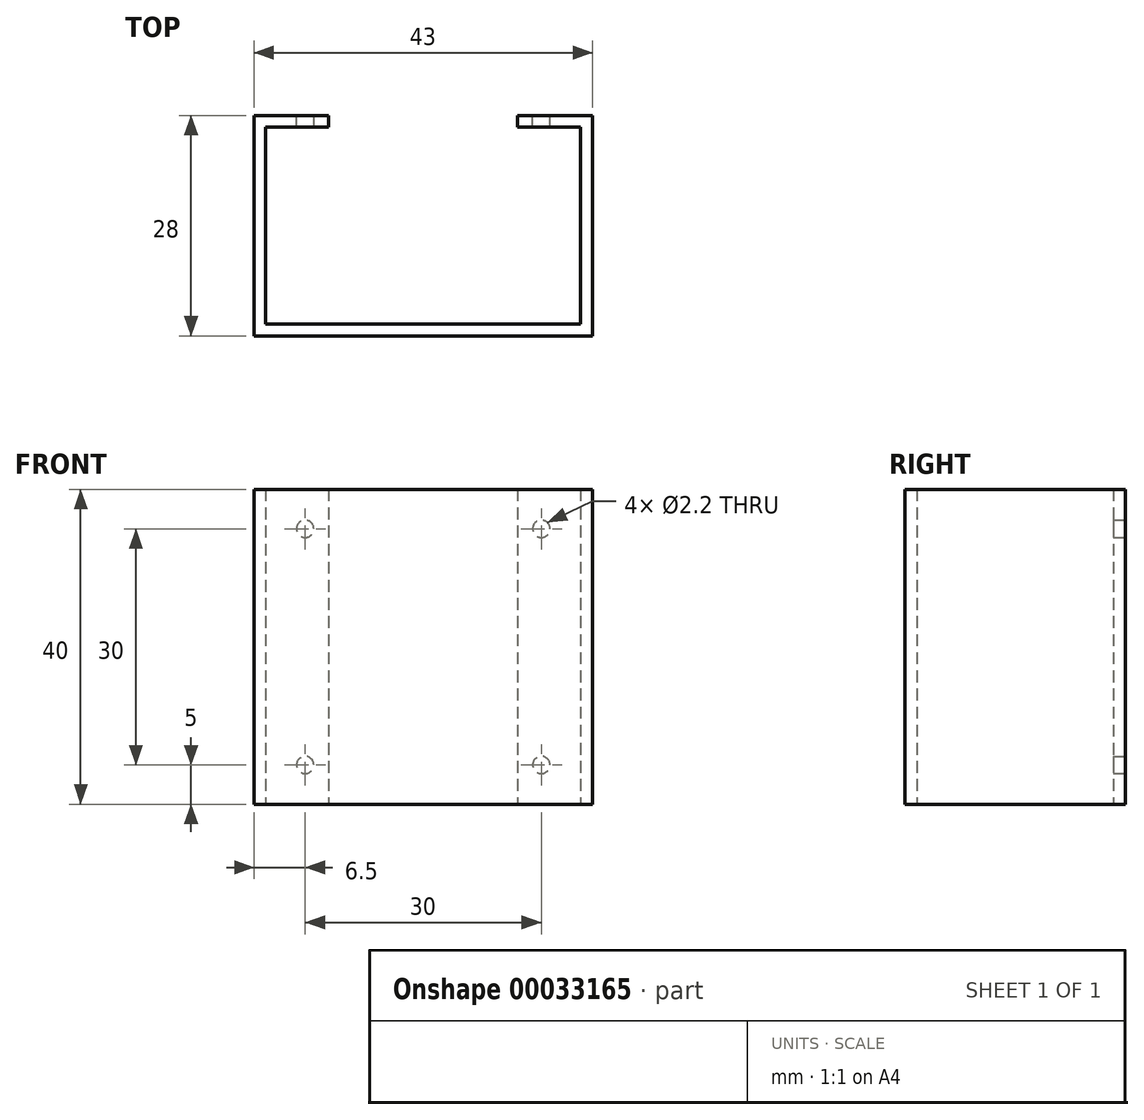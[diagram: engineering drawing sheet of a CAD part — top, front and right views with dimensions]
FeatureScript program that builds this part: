
annotation { "Feature Type Name" : "Feature", "Feature Type Description" : "" }
export const myFeature = defineFeature(function(context is Context, id is Id, definition is map)
    precondition{}
    {
        {
            var Q0;
            Q0=qCreatedBy(makeId("Top.planeOp"),FACE);
            var sketch = newSketch(context, id + "F0", { "sketchPlane" : qUnion([Q0])});
            skLineSegment(sketch, "E0.bottom", {"start": v(-21.5, 14) * mm, "end": v(-12, 14) * mm});
            skLineSegment(sketch, "E0.top", {"start": v(-21.5, -14) * mm, "end": v(21.5, -14) * mm});
            skLineSegment(sketch, "E0.left", {"start": v(-21.5, 14) * mm, "end": v(-21.5, -14) * mm});
            skLineSegment(sketch, "E0.right", {"start": v(21.5, 14) * mm, "end": v(21.5, -14) * mm});
            skPoint(sketch, "E0.middle", {"position": v(0, 0) * mm});
            skLineSegment(sketch, "E1.bottom", {"start": v(-20, 12.5) * mm, "end": v(-12, 12.5) * mm});
            skLineSegment(sketch, "E1.top", {"start": v(-20, -12.5) * mm, "end": v(20, -12.5) * mm});
            skLineSegment(sketch, "E1.left", {"start": v(-20, 12.5) * mm, "end": v(-20, -12.5) * mm});
            skLineSegment(sketch, "E1.right", {"start": v(20, 12.5) * mm, "end": v(20, -12.5) * mm});
            skLineSegment(sketch, "E2", {"start": v(-15, 14) * mm, "end": v(-15, 12.5) * mm, "construction": true});
            skLineSegment(sketch, "E3", {"start": v(-12, 14) * mm, "end": v(-12, 12.5) * mm});
            skLineSegment(sketch, "E4.MirrorCS", {"start": v(12, 14) * mm, "end": v(12, 12.5) * mm});
            skLineSegment(sketch, "E5.trimOffspring", {"start": v(12, 14) * mm, "end": v(21.5, 14) * mm});
            skLineSegment(sketch, "E6.trimOffspring", {"start": v(12, 12.5) * mm, "end": v(20, 12.5) * mm});
            skSolve(sketch);
        }
        {
            var Q0;
            Q0 = qSketchRegion(id + "F0", true);
            extrude(context, id + "F1", {"entities" : qUnion([Q0]), "depth" : 40 * mm});
        }
        {
            var Q0;
            Q0=makeQuery(id+"F1.opExtrude","SWEPT_FACE",FACE,{"disambiguationData":[OSD([sQuery(id+"F0.wireOp",EDGE,"E5.trimOffspring")])]});
            var sketch = newSketch(context, id + "F2", { "sketchPlane" : qUnion([Q0])});
            skLineSegment(sketch, "E7.0", {"start": v(21.5, 40) * mm, "end": v(21.5, 0) * mm, "construction": true});
            skLineSegment(sketch, "E8", {"start": v(-21.5, 20) * mm, "end": v(21.5, 20) * mm, "construction": true});
            skCircle(sketch, "E9", {"center": v(-15, 35) * mm, "radius": 1.1 * mm});
            skCircle(sketch, "E10.MirrorC", {"center": v(15, 35) * mm, "radius": 1.1 * mm});
            skCircle(sketch, "E11.MirrorC", {"center": v(-15, 5) * mm, "radius": 1.1 * mm});
            skCircle(sketch, "E12.MirrorC", {"center": v(15, 5) * mm, "radius": 1.1 * mm});
            skSolve(sketch);
        }
        {
            var Q0;
            Q0 = qSketchRegion(id + "F2", true);
            extrude(context, id + "F3", {"entities" : qUnion([Q0]), "operationType" : NewBodyOperationType.REMOVE, "endBound" : BoundingType.UP_TO_NEXT, "oppositeDirection" : true, "depth" : 25 * mm});
        }
    });
